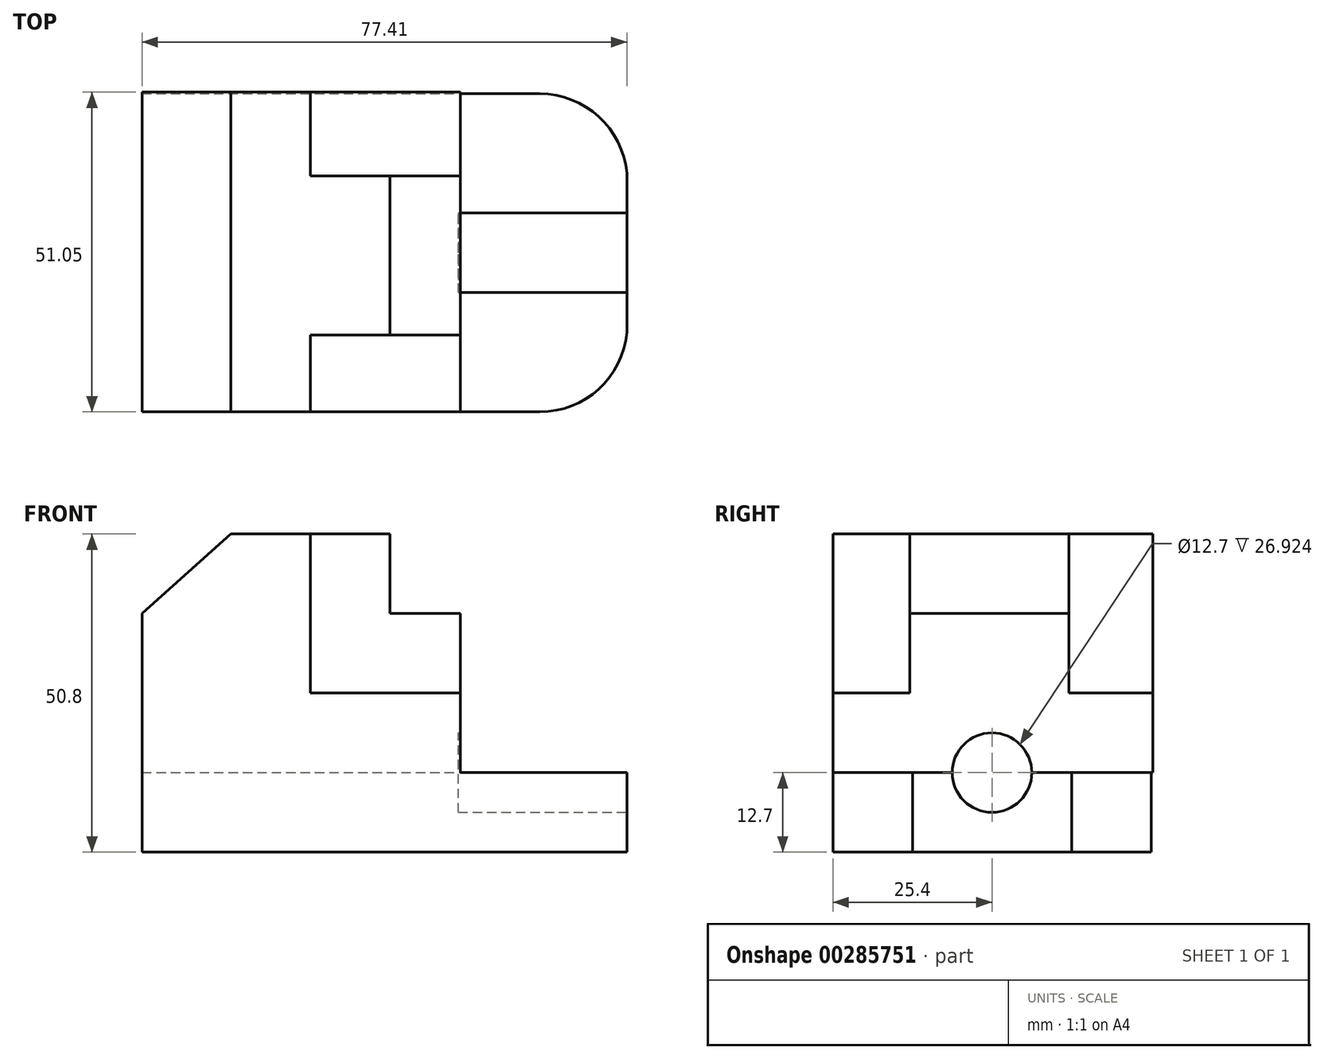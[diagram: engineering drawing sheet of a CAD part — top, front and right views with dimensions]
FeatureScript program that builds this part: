
annotation { "Feature Type Name" : "Feature", "Feature Type Description" : "" }
export const myFeature = defineFeature(function(context is Context, id is Id, definition is map)
    precondition{}
    {
        {
            var Q0;
            Q0=qCreatedBy(makeId("Top.planeOp"),FACE);
            var sketch = newSketch(context, id + "F0", { "sketchPlane" : qUnion([Q0])});
            skLineSegment(sketch, "E0", {"start": v(0, 0) * mm, "end": v(63.5, 0) * mm});
            skLineSegment(sketch, "E1", {"start": v(0, 0) * mm, "end": v(0, 50.8) * mm});
            skLineSegment(sketch, "E2", {"start": v(0, 50.8) * mm, "end": v(63.5, 50.8) * mm});
            skLineSegment(sketch, "E3", {"start": v(63.5, 50.8) * mm, "end": v(63.5, 0) * mm});
            skSolve(sketch);
        }
        {
            var Q0;
            Q0 = qSketchRegion(id + "F0", true);
            extrude(context, id + "F1", {"entities" : qUnion([Q0]), "depth" : 12.7 * mm});
        }
        {
            var Q0;
            Q0=makeQuery(id+"F1.opExtrude","CAP_FACE",FACE,{"disambiguationData":[OSD([sQuery(id+"F0.wireOp",EDGE,"E0"),sQuery(id+"F0.wireOp",EDGE,"E1"),sQuery(id+"F0.wireOp",EDGE,"E2"),sQuery(id+"F0.wireOp",EDGE,"E3")])],"isStart":false});
            var sketch = newSketch(context, id + "F2", { "sketchPlane" : qUnion([Q0])});
            skArc(sketch, "E4", {"start": v(77.41, 38.1) * mm, "mid": v(72.92, 47.15) * mm, "end": v(63.5, 50.8) * mm});
            skArc(sketch, "E5", {"start": v(63.5, 0) * mm, "mid": v(72.92, 3.65) * mm, "end": v(77.41, 12.7) * mm});
            skLineSegment(sketch, "E6", {"start": v(63.5, 50.8) * mm, "end": v(63.5, 0) * mm});
            skLineSegment(sketch, "E7", {"start": v(77.41, 38.1) * mm, "end": v(77.41, 12.7) * mm});
            skSolve(sketch);
        }
        {
            var Q0;
            Q0=makeQuery(id+"F2.imprint","IMPRINT",FACE,{"disambiguationData":[TD([[makeQuery(id+"F2.imprint","IMPRINT",EDGE,{"derivedFrom":sQuery(id+"F2.wireOp",EDGE,"E4")}),1.0]])]});
            extrude(context, id + "F3", {"entities" : qUnion([Q0]), "operationType" : NewBodyOperationType.ADD, "oppositeDirection" : true, "depth" : 12.7 * mm});
        }
        {
            var Q0;
            Q0=makeQuery(id+"F1.opExtrude","SWEPT_FACE",FACE,{"disambiguationData":[OSD([sQuery(id+"F0.wireOp",EDGE,"E0")])]});
            var sketch = newSketch(context, id + "F4", { "sketchPlane" : qUnion([Q0])});
            skLineSegment(sketch, "E8", {"start": v(0, 12.7) * mm, "end": v(0, 38.1) * mm});
            skLineSegment(sketch, "E9", {"start": v(0, 38.1) * mm, "end": v(14.2, 50.8) * mm});
            skLineSegment(sketch, "E10", {"start": v(14.2, 50.8) * mm, "end": v(26.9, 50.8) * mm});
            skLineSegment(sketch, "E11", {"start": v(26.9, 50.8) * mm, "end": v(26.9, 25.4) * mm});
            skLineSegment(sketch, "E12", {"start": v(26.9, 25.4) * mm, "end": v(50.8, 25.4) * mm});
            skLineSegment(sketch, "E13", {"start": v(50.8, 25.4) * mm, "end": v(50.8, 12.7) * mm});
            skLineSegment(sketch, "E14", {"start": v(50.8, 12.7) * mm, "end": v(0, 12.7) * mm});
            skSolve(sketch);
        }
        {
            var Q0;
            Q0 = qSketchRegion(id + "F4", true);
            extrude(context, id + "F5", {"entities" : qUnion([Q0]), "operationType" : NewBodyOperationType.ADD, "oppositeDirection" : true, "depth" : 51.05 * mm});
        }
        {
            var Q0;
            Q0=makeQuery(id+"F5.opExtrude","SWEPT_FACE",FACE,{"disambiguationData":[OSD([sQuery(id+"F4.wireOp",EDGE,"E12")])]});
            var sketch = newSketch(context, id + "F6", { "sketchPlane" : qUnion([Q0])});
            skLineSegment(sketch, "E15", {"start": v(26.9, 37.66) * mm, "end": v(39.6, 37.66) * mm});
            skLineSegment(sketch, "E16", {"start": v(39.6, 37.66) * mm, "end": v(39.6, 12.26) * mm});
            skLineSegment(sketch, "E17", {"start": v(39.6, 12.26) * mm, "end": v(26.9, 12.26) * mm});
            skLineSegment(sketch, "E18", {"start": v(26.9, 12.26) * mm, "end": v(26.9, 37.66) * mm});
            skSolve(sketch);
        }
        {
            var Q0;
            Q0 = qSketchRegion(id + "F6", true);
            extrude(context, id + "F7", {"entities" : qUnion([Q0]), "operationType" : NewBodyOperationType.ADD, "depth" : 25.4 * mm});
        }
        {
            var Q0;
            Q0=makeQuery(id+"F5.opExtrude","SWEPT_FACE",FACE,{"disambiguationData":[OSD([sQuery(id+"F4.wireOp",EDGE,"E12")])]});
            var sketch = newSketch(context, id + "F8", { "sketchPlane" : qUnion([Q0])});
            skLineSegment(sketch, "E19", {"start": v(39.6, 37.66) * mm, "end": v(50.8, 37.66) * mm});
            skLineSegment(sketch, "E20", {"start": v(50.8, 37.66) * mm, "end": v(50.8, 12.26) * mm});
            skLineSegment(sketch, "E21", {"start": v(50.8, 12.26) * mm, "end": v(39.6, 12.26) * mm});
            skSolve(sketch);
        }
        {
            var Q0;
            Q0 = qSketchRegion(id + "F8", true);
            var Q1;
            Q1=makeQuery(id+"F8.imprint","IMPRINT",FACE,{"disambiguationData":[TD([[makeQuery(id+"F8.imprint","IMPRINT",EDGE,{"derivedFrom":sQuery(id+"F8.wireOp",EDGE,"E19")}),-1.0]])]});
            extrude(context, id + "F9", {"entities" : qUnion([Q0, Q1]), "operationType" : NewBodyOperationType.ADD, "depth" : 12.7 * mm});
        }
        {
            var Q0;
            Q0=makeQuery(id+"F3.opExtrude","SWEPT_FACE",FACE,{"disambiguationData":[OSD([sQuery(id+"F2.wireOp",EDGE,"E7")])]});
            var sketch = newSketch(context, id + "F10", { "sketchPlane" : qUnion([Q0])});
            skCircle(sketch, "E22", {"center": v(25.4, 12.7) * mm, "radius": 6.35 * mm});
            skSolve(sketch);
        }
        {
            var Q0;
            Q0 = qSketchRegion(id + "F10", true);
            extrude(context, id + "F11", {"entities" : qUnion([Q0]), "operationType" : NewBodyOperationType.REMOVE, "oppositeDirection" : true, "depth" : 26.92 * mm});
        }
    });
